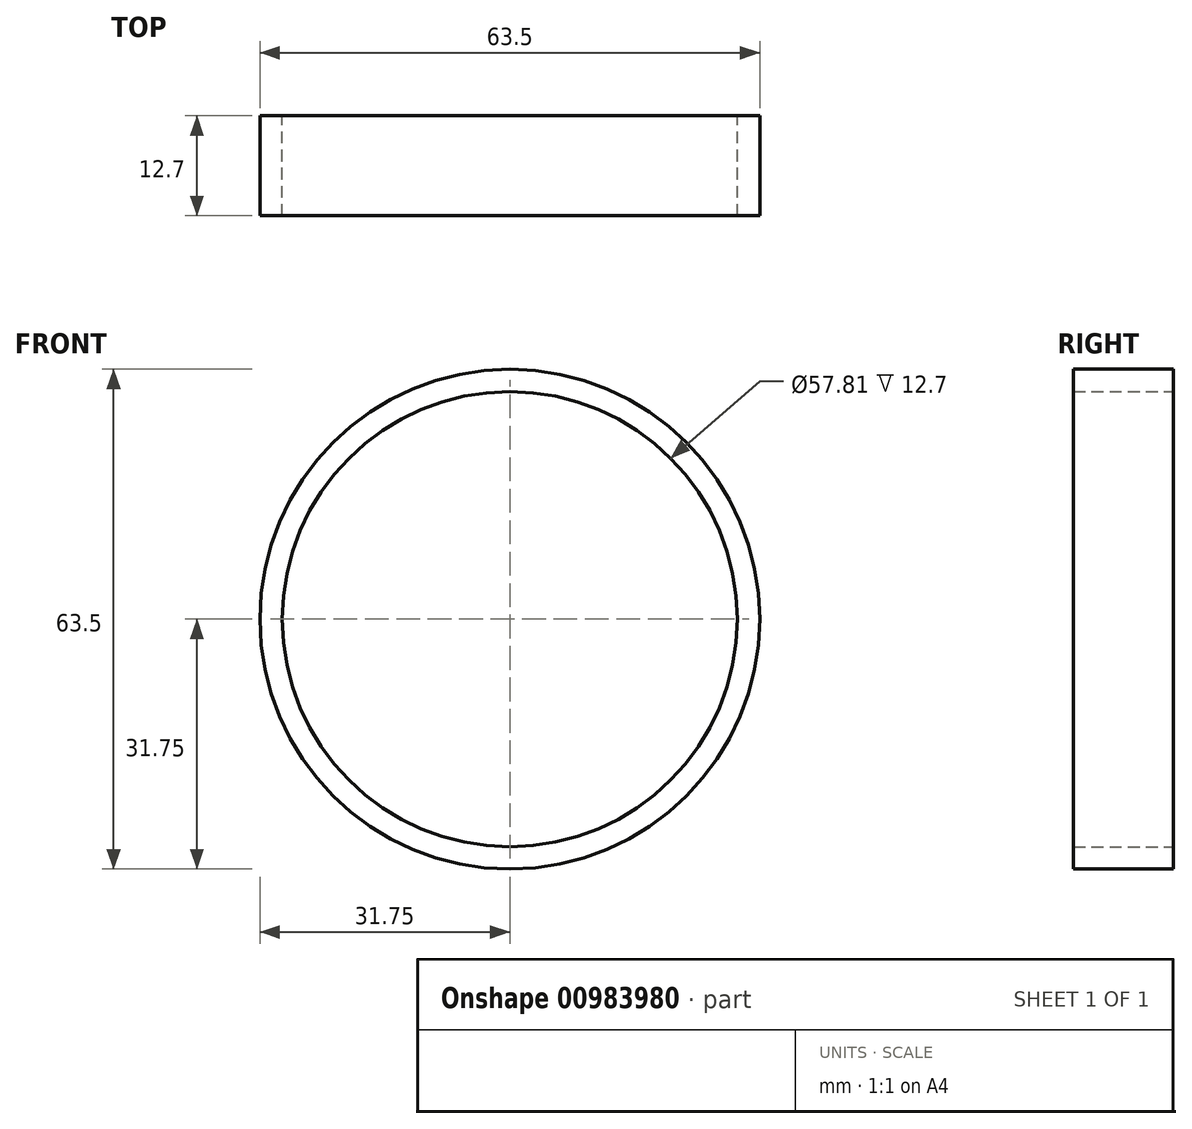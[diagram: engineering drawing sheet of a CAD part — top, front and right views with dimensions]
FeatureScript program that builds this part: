
annotation { "Feature Type Name" : "Feature", "Feature Type Description" : "" }
export const myFeature = defineFeature(function(context is Context, id is Id, definition is map)
    precondition{}
    {
        {
            var Q0;
            Q0=qCreatedBy(makeId("Front.planeOp"),FACE);
            var sketch = newSketch(context, id + "F0", { "sketchPlane" : qUnion([Q0])});
            skCircle(sketch, "E0", {"center": v(0, 0) * mm, "radius": 31.75 * mm});
            skCircle(sketch, "E1", {"center": v(0, 0) * mm, "radius": 28.9 * mm});
            skSolve(sketch);
        }
        {
            var Q0;
            Q0 = qSketchRegion(id + "F0", true);
            extrude(context, id + "F1", {"entities" : qUnion([Q0]), "depth" : 12.7 * mm, "offsetDistance" : 25.4 * mm});
        }
    });
